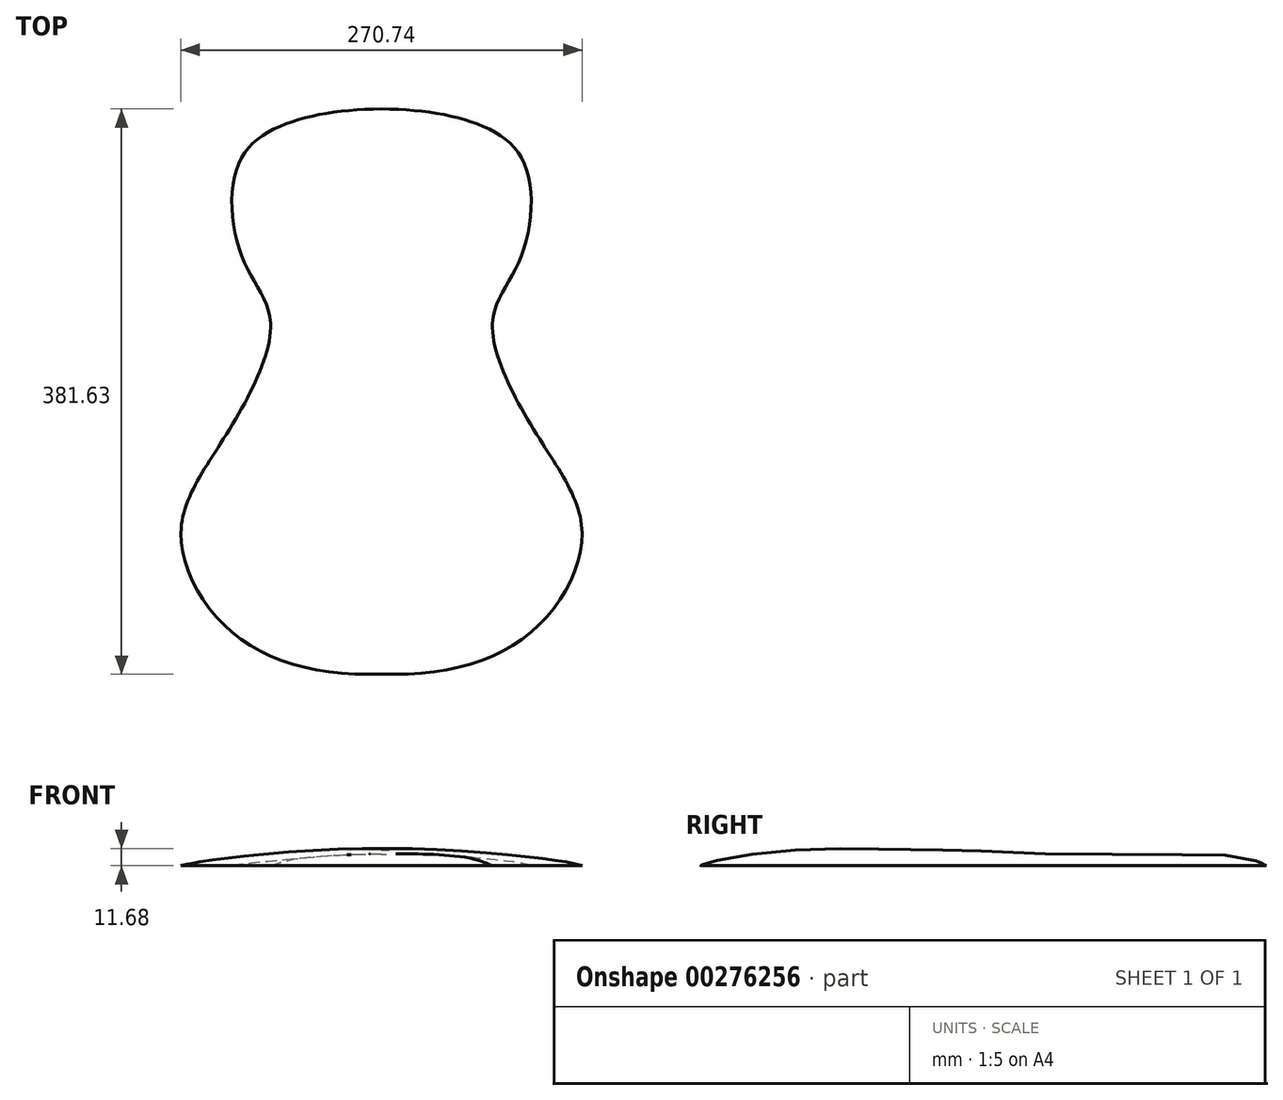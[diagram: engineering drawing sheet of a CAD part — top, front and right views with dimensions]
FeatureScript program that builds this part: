
annotation { "Feature Type Name" : "Feature", "Feature Type Description" : "" }
export const myFeature = defineFeature(function(context is Context, id is Id, definition is map)
    precondition{}
    {
        {
            var Q0;
            Q0=qCreatedBy(makeId("Top.planeOp"),FACE);
            var sketch = newSketch(context, id + "F0", { "sketchPlane" : qUnion([Q0])});
            skFitSpline(sketch, "E0", {"points": [v(0, 144.66) * mm, v(-63, 135.15) * mm, v(-96.43, 107.76) * mm, v(-93.9, 44.37) * mm, v(-74.88, 0) * mm, v(-106.7, -78.23) * mm, v(-135.35, -141.55) * mm, v(-100.68, -208.64) * mm, v(0, -236.8) * mm], "startDerivative": vector(-596.27, -3.99) * mm, "endDerivative": vector(789.17, 29.17) * mm});
            skLineSegment(sketch, "E1", {"start": v(0, 71.6) * mm, "end": v(0, -48.54) * mm, "construction": true});
            skFitSpline(sketch, "E2.MirrorCS", {"points": [v(0, 144.66) * mm, v(63, 135.15) * mm, v(96.43, 107.76) * mm, v(93.9, 44.37) * mm, v(74.88, 0) * mm, v(106.7, -78.23) * mm, v(135.35, -141.55) * mm, v(100.68, -208.64) * mm, v(0, -236.8) * mm], "startDerivative": vector(596.27, -3.99) * mm, "endDerivative": vector(-789.17, 29.17) * mm});
            skSolve(sketch);
        }
        {
            var Q0;
            Q0=qCreatedBy(makeId("Front.planeOp"),FACE);
            var sketch = newSketch(context, id + "F1", { "sketchPlane" : qUnion([Q0])});
            skFitSpline(sketch, "E3", {"points": [v(-74.88, 0) * mm, v(-59.3, 4.3) * mm, v(0, 8.05) * mm, v(59.63, 5.13) * mm, v(74.88, 0) * mm], "startDerivative": vector(76.86, 26.72) * mm, "endDerivative": vector(71.25, -33.71) * mm});
            skSolve(sketch);
        }
        {
            var Q0;
            Q0=qCreatedBy(makeId("Front.planeOp"),FACE);
            var Q1;
            Q1=sQuery(id+"F0.wireOp",VERTEX,"E0.5.internal");
            cPlane(context, id + "F2", {"entities" : qUnion([Q0, Q1]), "cplaneType" : CPlaneType.PLANE_POINT, "offset" : 25.4 * mm, "width" : 152.4 * mm, "height" : 152.4 * mm});
        }
        {
            var Q0;
            Q0=qCreatedBy(id+"F2.planeOp",FACE);
            var sketch = newSketch(context, id + "F3", { "sketchPlane" : qUnion([Q0])});
            skFitSpline(sketch, "E4", {"points": [v(-106.7, 0) * mm, v(-59.3, 6.85) * mm, v(0, 10.59) * mm, v(59.63, 7.67) * mm, v(106.7, 0) * mm], "startDerivative": vector(76.86, 26.72) * mm, "endDerivative": vector(71.25, -33.71) * mm});
            skSolve(sketch);
        }
        {
            var Q0;
            Q0=qCreatedBy(makeId("Front.planeOp"),FACE);
            var Q1;
            Q1=sQuery(id+"F0.wireOp",VERTEX,"E2.MirrorCS.2.internal");
            cPlane(context, id + "F4", {"entities" : qUnion([Q0, Q1]), "cplaneType" : CPlaneType.PLANE_POINT, "offset" : 25.4 * mm, "width" : 152.4 * mm, "height" : 152.4 * mm});
        }
        {
            var Q0;
            Q0=qCreatedBy(id+"F4.planeOp",FACE);
            var sketch = newSketch(context, id + "F5", { "sketchPlane" : qUnion([Q0])});
            skFitSpline(sketch, "E5", {"points": [v(-96.43, 0) * mm, v(-59.3, 3.66) * mm, v(0, 7.4) * mm, v(59.63, 4.48) * mm, v(96.43, 0) * mm], "startDerivative": vector(76.86, 26.72) * mm, "endDerivative": vector(71.25, -33.71) * mm});
            skSolve(sketch);
        }
        {
            var Q0;
            Q0=qCreatedBy(makeId("Front.planeOp"),FACE);
            var Q1;
            Q1=sQuery(id+"F0.wireOp",VERTEX,"E2.MirrorCS.6.internal");
            cPlane(context, id + "F6", {"entities" : qUnion([Q0, Q1]), "cplaneType" : CPlaneType.PLANE_POINT, "offset" : 25.4 * mm, "width" : 152.4 * mm, "height" : 152.4 * mm});
        }
        {
            var Q0;
            Q0=qCreatedBy(id+"F6.planeOp",FACE);
            var sketch = newSketch(context, id + "F7", { "sketchPlane" : qUnion([Q0])});
            skFitSpline(sketch, "E6", {"points": [v(-135.35, 0) * mm, v(-72.16, 8.42) * mm, v(0, 11.67) * mm, v(73.01, 8.42) * mm, v(135.35, 0) * mm], "startDerivative": vector(76.86, 26.72) * mm, "endDerivative": vector(71.25, -33.71) * mm});
            skSolve(sketch);
        }
        {
            var Q0;
            Q0=makeQuery(id+"F0.imprint","IMPRINT",FACE,{"disambiguationData":[TD([[makeQuery(id+"F0.imprint","IMPRINT",EDGE,{"derivedFrom":sQuery(id+"F0.wireOp",EDGE,"E0")}),1.0]])]});
            var Q1;
            Q1=sQuery(id+"F0.wireOp",EDGE,"E0");
            var Q2;
            Q2=sQuery(id+"F0.wireOp",EDGE,"E2.MirrorCS");
            var Q3;
            Q3=sQuery(id+"F5.wireOp",EDGE,"E5");
            var Q4;
            Q4=sQuery(id+"F1.wireOp",EDGE,"E3");
            var Q5;
            Q5=sQuery(id+"F3.wireOp",EDGE,"E4");
            var Q6;
            Q6=sQuery(id+"F7.wireOp",EDGE,"E6");
            loft(context, id + "F8", {"bodyType" : ToolBodyType.SURFACE, "addGuides" : true, "sheetProfilesArray" : [{ "sheetProfileEntities" : qUnion([Q0]) }], "wireProfilesArray" : [{ "wireProfileEntities" : qUnion([Q1]) }, { "wireProfileEntities" : qUnion([Q2]) }], "guidesArray" : [{ "guideEntities" : qUnion([Q3]), "guideDerivativeType" : LoftGuideDerivativeType.DEFAULT, "guideDerivativeMagnitude" : 1 }, { "guideEntities" : qUnion([Q4]), "guideDerivativeType" : LoftGuideDerivativeType.DEFAULT, "guideDerivativeMagnitude" : 1 }, { "guideEntities" : qUnion([Q5]), "guideDerivativeType" : LoftGuideDerivativeType.DEFAULT, "guideDerivativeMagnitude" : 1 }, { "guideEntities" : qUnion([Q6]), "guideDerivativeType" : LoftGuideDerivativeType.DEFAULT, "guideDerivativeMagnitude" : 1 }]});
        }
    });
